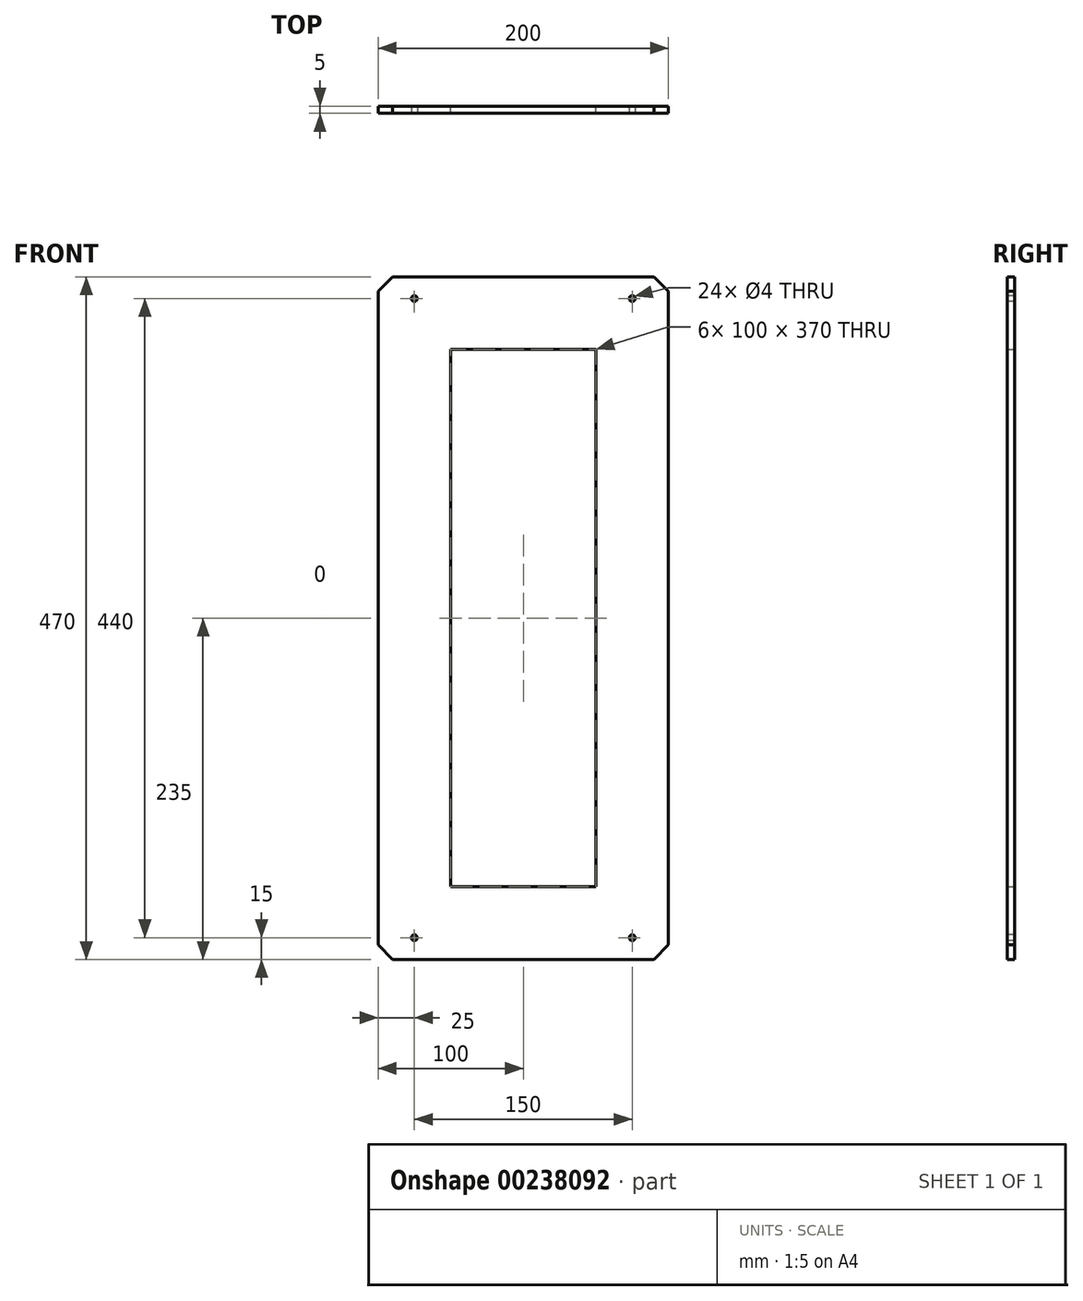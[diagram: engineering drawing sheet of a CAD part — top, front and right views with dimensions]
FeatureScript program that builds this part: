
annotation { "Feature Type Name" : "Feature", "Feature Type Description" : "" }
export const myFeature = defineFeature(function(context is Context, id is Id, definition is map)
    precondition{}
    {
        {
            var Q0;
            Q0=qCreatedBy(makeId("Front.planeOp"),FACE);
            var sketch = newSketch(context, id + "F0", { "sketchPlane" : qUnion([Q0])});
            skLineSegment(sketch, "E0.bottom", {"start": v(-100, 235) * mm, "end": v(100, 235) * mm});
            skLineSegment(sketch, "E0.top", {"start": v(-100, -235) * mm, "end": v(100, -235) * mm});
            skLineSegment(sketch, "E0.left", {"start": v(-100, 235) * mm, "end": v(-100, -235) * mm});
            skLineSegment(sketch, "E0.right", {"start": v(100, 235) * mm, "end": v(100, -235) * mm});
            skPoint(sketch, "E0.middle", {"position": v(0, 0) * mm});
            skLineSegment(sketch, "E1.bottom", {"start": v(50, 185) * mm, "end": v(-50, 185) * mm});
            skLineSegment(sketch, "E1.top", {"start": v(50, -185) * mm, "end": v(-50, -185) * mm});
            skLineSegment(sketch, "E1.left", {"start": v(50, 185) * mm, "end": v(50, -185) * mm});
            skLineSegment(sketch, "E1.right", {"start": v(-50, 185) * mm, "end": v(-50, -185) * mm});
            skSolve(sketch);
        }
        {
            var Q0;
            Q0=makeQuery(id+"F0.imprint","IMPRINT",FACE,{"disambiguationData":[TD([[makeQuery(id+"F0.imprint","IMPRINT",EDGE,{"derivedFrom":sQuery(id+"F0.wireOp",EDGE,"E0.bottom")}),-1.0]])]});
            extrude(context, id + "F1", {"entities" : qUnion([Q0]), "depth" : 5 * mm});
        }
        {
            var Q0;
            Q0=makeQuery(id+"F1.opExtrude","SWEPT_EDGE",EDGE,{"disambiguationData":[OSD([sQuery(id+"F0.wireOp",EDGE,"E0.bottom"),sQuery(id+"F0.wireOp",EDGE,"E0.left")])]});
            var Q1;
            Q1=makeQuery(id+"F1.opExtrude","SWEPT_EDGE",EDGE,{"disambiguationData":[OSD([sQuery(id+"F0.wireOp",EDGE,"E0.bottom"),sQuery(id+"F0.wireOp",EDGE,"E0.right")])]});
            var Q2;
            Q2=makeQuery(id+"F1.opExtrude","SWEPT_EDGE",EDGE,{"disambiguationData":[OSD([sQuery(id+"F0.wireOp",EDGE,"E0.top"),sQuery(id+"F0.wireOp",EDGE,"E0.right")])]});
            var Q3;
            Q3=makeQuery(id+"F1.opExtrude","SWEPT_EDGE",EDGE,{"disambiguationData":[OSD([sQuery(id+"F0.wireOp",EDGE,"E0.top"),sQuery(id+"F0.wireOp",EDGE,"E0.left")])]});
            chamfer(context, id + "F2", {"entities" : qUnion([Q0, Q1, Q2, Q3]), "width" : 10 * mm, "tangentPropagation" : true});
        }
        {
            var Q0;
            Q0=makeQuery(id+"F1.opExtrude","CAP_FACE",FACE,{"disambiguationData":[OSD([sQuery(id+"F0.wireOp",EDGE,"E0.bottom"),sQuery(id+"F0.wireOp",EDGE,"E0.top"),sQuery(id+"F0.wireOp",EDGE,"E0.left"),sQuery(id+"F0.wireOp",EDGE,"E0.right"),sQuery(id+"F0.wireOp",EDGE,"E1.bottom"),sQuery(id+"F0.wireOp",EDGE,"E1.top"),sQuery(id+"F0.wireOp",EDGE,"E1.left"),sQuery(id+"F0.wireOp",EDGE,"E1.right")])],"isStart":false});
            var sketch = newSketch(context, id + "F3", { "sketchPlane" : qUnion([Q0])});
            skLineSegment(sketch, "E2.bottom", {"start": v(75, 220) * mm, "end": v(-75, 220) * mm});
            skLineSegment(sketch, "E2.top", {"start": v(75, -220) * mm, "end": v(-75, -220) * mm});
            skLineSegment(sketch, "E2.left", {"start": v(75, 220) * mm, "end": v(75, -220) * mm});
            skLineSegment(sketch, "E2.right", {"start": v(-75, 220) * mm, "end": v(-75, -220) * mm});
            skPoint(sketch, "E2.middle", {"position": v(0, 0) * mm});
            skSolve(sketch);
        }
        {
            var Q0;
            Q0=sQuery(id+"F3.wireOp",VERTEX,"E2.right.start");
            var Q1;
            Q1=sQuery(id+"F3.wireOp",VERTEX,"E2.bottom.start");
            var Q2;
            Q2=sQuery(id+"F3.wireOp",VERTEX,"E2.right.end");
            var Q3;
            Q3=sQuery(id+"F3.wireOp",VERTEX,"E2.left.end");
            var Q4;
            Q4=makeQuery(id+"F1.opExtrude","SWEPT_BODY",BODY,{"disambiguationData":[OSD([sQuery(id+"F0.wireOp",EDGE,"E0.bottom"),sQuery(id+"F0.wireOp",EDGE,"E0.top"),sQuery(id+"F0.wireOp",EDGE,"E0.left"),sQuery(id+"F0.wireOp",EDGE,"E0.right"),sQuery(id+"F0.wireOp",EDGE,"E1.bottom"),sQuery(id+"F0.wireOp",EDGE,"E1.top"),sQuery(id+"F0.wireOp",EDGE,"E1.left"),sQuery(id+"F0.wireOp",EDGE,"E1.right")])]});
            hole(context, id + "F4", {"style" : HoleStyle.SIMPLE, "endStyle" : HoleEndStyle.BLIND, "holeDiameter" : 4 * mm, "holeDepth" : 8 * mm, "startFromSketch" : true, "locations" : qUnion([Q0, Q1, Q2, Q3]), "scope" : qUnion([Q4])});
        }
    });
